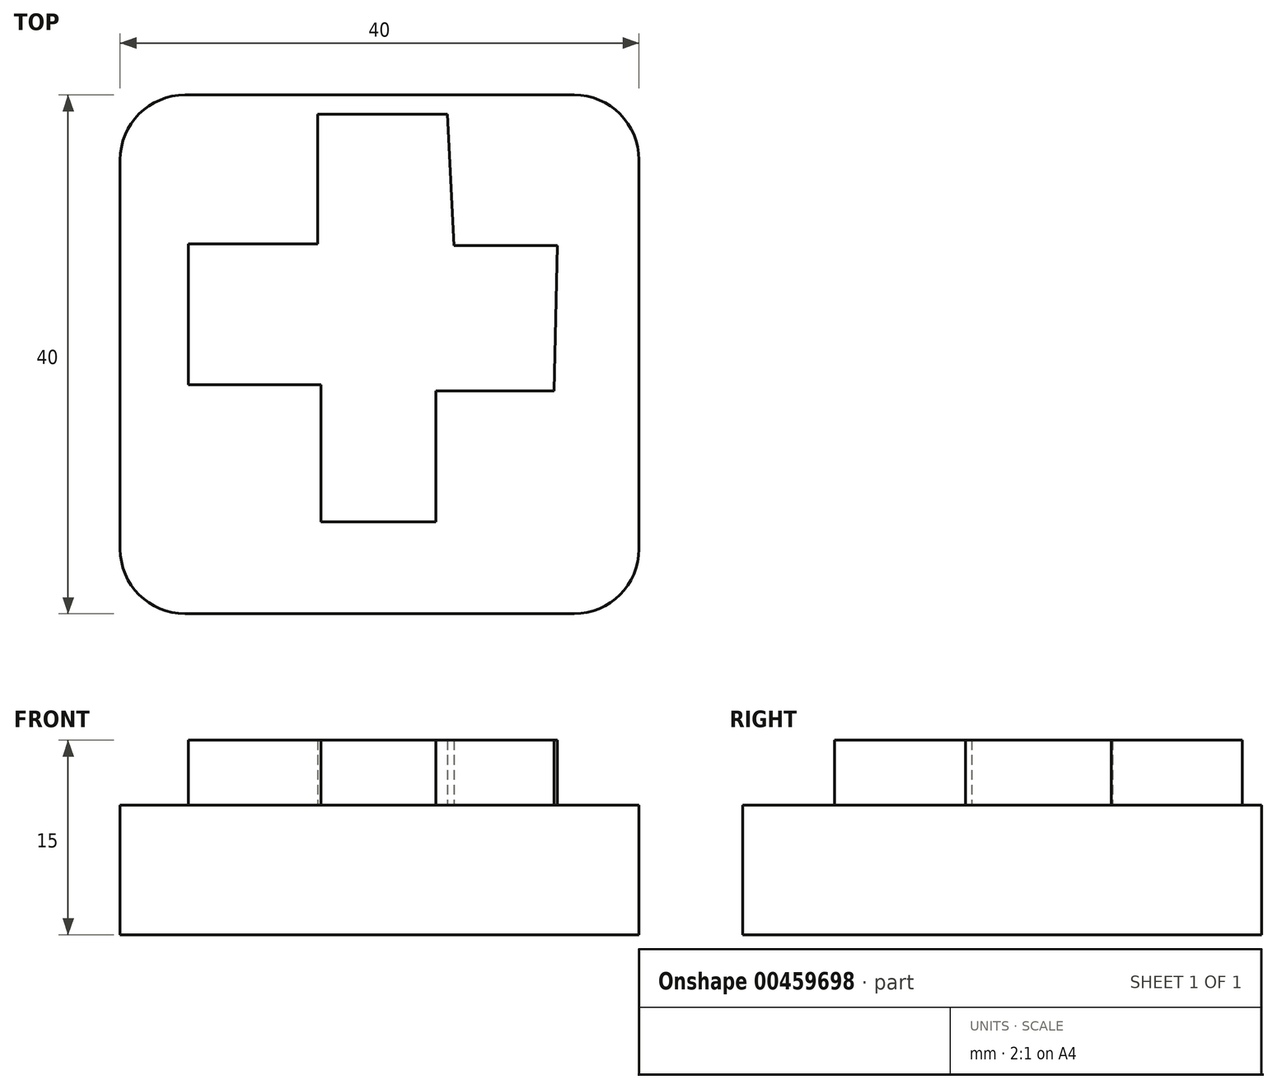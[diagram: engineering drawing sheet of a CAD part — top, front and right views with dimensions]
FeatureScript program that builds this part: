
annotation { "Feature Type Name" : "Feature", "Feature Type Description" : "" }
export const myFeature = defineFeature(function(context is Context, id is Id, definition is map)
    precondition{}
    {
        {
            var Q0;
            Q0=qCreatedBy(makeId("Top.planeOp"),FACE);
            var sketch = newSketch(context, id + "F0", { "sketchPlane" : qUnion([Q0])});
            skLineSegment(sketch, "E0.bottom", {"start": v(5, 0) * mm, "end": v(35, 0) * mm});
            skLineSegment(sketch, "E0.top", {"start": v(5, 40) * mm, "end": v(35, 40) * mm});
            skLineSegment(sketch, "E0.left", {"start": v(0, 5) * mm, "end": v(0, 35) * mm});
            skLineSegment(sketch, "E0.right", {"start": v(40, 5) * mm, "end": v(40, 35) * mm});
            skPoint(sketch, "E0.middle", {"position": v(20, 20) * mm});
            skPoint(sketch, "E1.visualSharp", {"position": v(0, 40) * mm});
            skArc(sketch, "E1.filletArc", {"start": v(5, 40) * mm, "mid": v(1.46, 38.54) * mm, "end": v(0, 35) * mm});
            skPoint(sketch, "E2.visualSharp", {"position": v(0, 0) * mm});
            skArc(sketch, "E2.filletArc", {"start": v(0, 5) * mm, "mid": v(1.46, 1.46) * mm, "end": v(5, 0) * mm});
            skPoint(sketch, "E3.visualSharp", {"position": v(40, 0) * mm});
            skArc(sketch, "E3.filletArc", {"start": v(35, 0) * mm, "mid": v(38.54, 1.46) * mm, "end": v(40, 5) * mm});
            skPoint(sketch, "E4.visualSharp", {"position": v(40, 40) * mm});
            skArc(sketch, "E4.filletArc", {"start": v(40, 35) * mm, "mid": v(38.54, 38.54) * mm, "end": v(35, 40) * mm});
            skSolve(sketch);
        }
        {
            var Q0;
            Q0 = qSketchRegion(id + "F0", true);
            extrude(context, id + "F1", {"entities" : qUnion([Q0]), "depth" : 10 * mm});
        }
        {
            var Q0;
            Q0=makeQuery(id+"F1.opExtrude","CAP_FACE",FACE,{"disambiguationData":[OSD([sQuery(id+"F0.wireOp",EDGE,"E0.bottom"),sQuery(id+"F0.wireOp",EDGE,"E0.top"),sQuery(id+"F0.wireOp",EDGE,"E0.left"),sQuery(id+"F0.wireOp",EDGE,"E0.right"),sQuery(id+"F0.wireOp",EDGE,"E1.filletArc"),sQuery(id+"F0.wireOp",EDGE,"E2.filletArc"),sQuery(id+"F0.wireOp",EDGE,"E3.filletArc"),sQuery(id+"F0.wireOp",EDGE,"E4.filletArc")])],"isStart":false});
            var sketch = newSketch(context, id + "F2", { "sketchPlane" : qUnion([Q0])});
            skLineSegment(sketch, "E5", {"start": v(25.24, 38.5) * mm, "end": v(15.24, 38.5) * mm});
            skLineSegment(sketch, "E6", {"start": v(15.24, 38.5) * mm, "end": v(15.24, 28.5) * mm});
            skLineSegment(sketch, "E7", {"start": v(15.24, 28.5) * mm, "end": v(5.24, 28.5) * mm});
            skLineSegment(sketch, "E8", {"start": v(5.24, 28.5) * mm, "end": v(5.24, 17.64) * mm});
            skLineSegment(sketch, "E9", {"start": v(5.24, 17.64) * mm, "end": v(15.47, 17.64) * mm});
            skLineSegment(sketch, "E10", {"start": v(15.47, 17.64) * mm, "end": v(15.47, 7.09) * mm});
            skLineSegment(sketch, "E11", {"start": v(15.47, 7.09) * mm, "end": v(24.34, 7.09) * mm});
            skLineSegment(sketch, "E12", {"start": v(24.34, 7.09) * mm, "end": v(24.34, 17.18) * mm});
            skLineSegment(sketch, "E13", {"start": v(24.34, 17.18) * mm, "end": v(33.46, 17.18) * mm});
            skLineSegment(sketch, "E14", {"start": v(33.46, 17.18) * mm, "end": v(33.71, 28.4) * mm});
            skLineSegment(sketch, "E15", {"start": v(33.71, 28.4) * mm, "end": v(25.73, 28.4) * mm});
            skLineSegment(sketch, "E16", {"start": v(25.73, 28.4) * mm, "end": v(25.24, 38.5) * mm});
            skSolve(sketch);
        }
        {
            var Q0;
            Q0=makeQuery(id+"F2.imprint","IMPRINT",FACE,{"disambiguationData":[TD([[makeQuery(id+"F2.imprint","IMPRINT",EDGE,{"derivedFrom":sQuery(id+"F2.wireOp",EDGE,"E5")}),1.0]])]});
            extrude(context, id + "F3", {"entities" : qUnion([Q0]), "operationType" : NewBodyOperationType.ADD, "depth" : 5 * mm});
        }
    });
